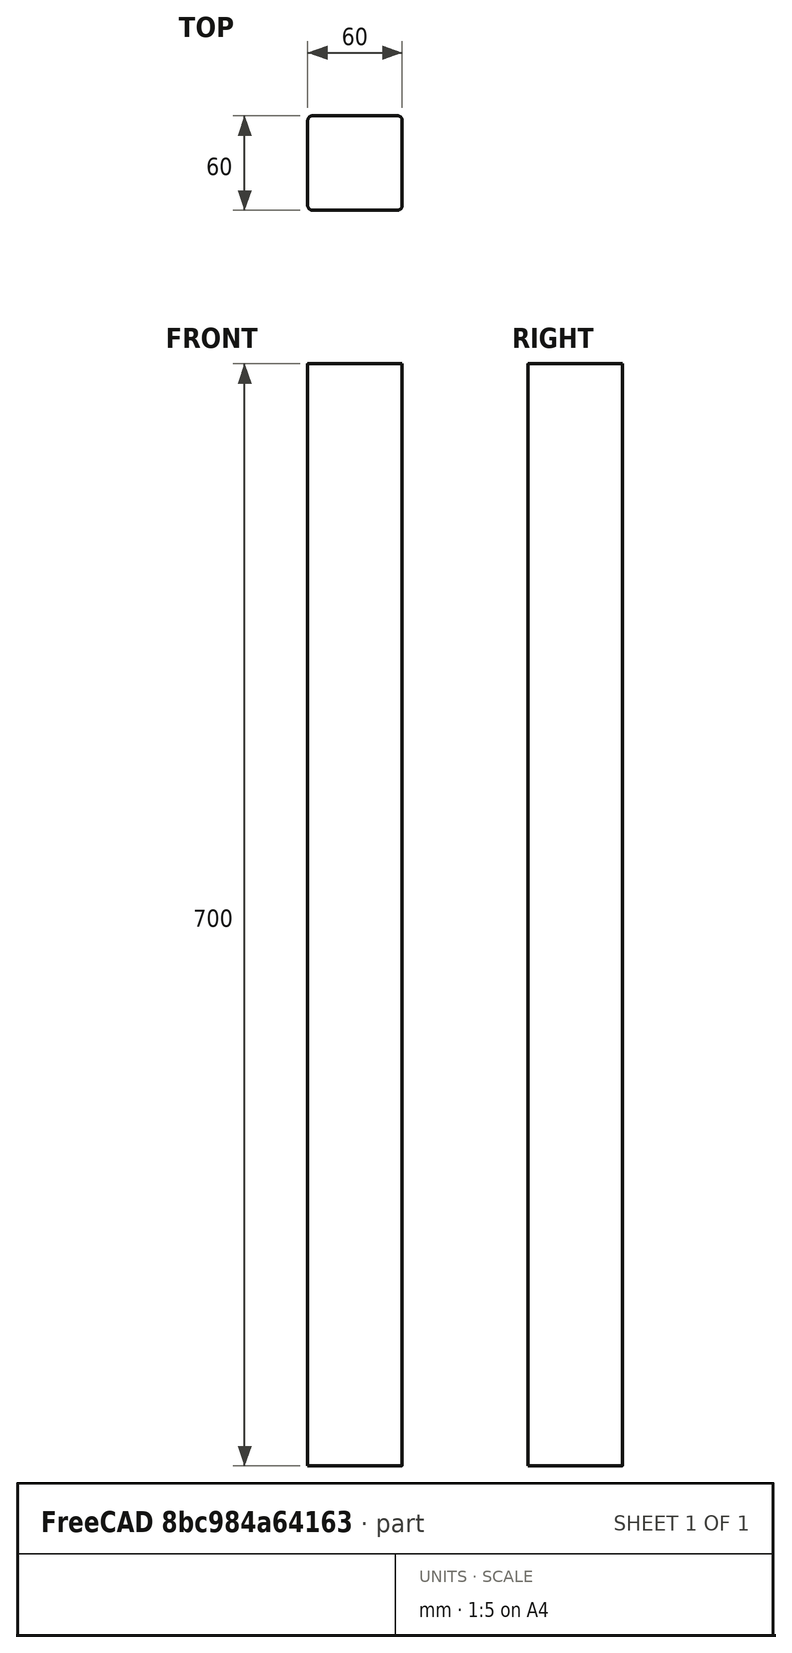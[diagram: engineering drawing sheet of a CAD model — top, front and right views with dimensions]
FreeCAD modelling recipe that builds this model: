
FCSTD DOCUMENT  (FreeCAD 0.19R)
Label: column_60_60
License: All rights reserved
LicenseURL: http://en.wikipedia.org/wiki/All_rights_reserved
objects: PartDesign::CoordinateSystem×7, Sketcher::SketchObject×1, PartDesign::Pad×1, PartDesign::Body×1
note: 11 computed .brp shape members not serialized (recipe doc carries the construction recipe); baked Part::Feature solids carry a one-line shape summary decoded from their .brp

FEATURE [PartDesign::CoordinateSystem] LCS_0
  AttacherType = Attacher::AttachEngine3D
  MapMode = 2
  Support = -> [X_Axis]
FEATURE [Sketcher::SketchObject] Sketch
  FullyConstrained = true
  MapMode = 5
  Support = -> [XY_Plane]
  sketch-geometry (8):
    g0: LineSegment StartX=-27 StartY=30 StartZ=0 EndX=27 EndY=30 EndZ=0
    g1: LineSegment StartX=30 StartY=27 StartZ=0 EndX=30 EndY=-27 EndZ=0
    g2: LineSegment StartX=27 StartY=-30 StartZ=0 EndX=-27 EndY=-30 EndZ=0
    g3: LineSegment StartX=-30 StartY=-27 StartZ=0 EndX=-30 EndY=27 EndZ=0
    g4: ArcOfCircle CenterX=-27 CenterY=27 CenterZ=0 NormalX=0 NormalY=0 NormalZ=1 AngleXU=0 Radius=3 StartAngle=1.5708 EndAngle=3.14159
    g5: ArcOfCircle CenterX=-27 CenterY=-27 CenterZ=0 NormalX=0 NormalY=0 NormalZ=1 AngleXU=0 Radius=3 StartAngle=3.14159 EndAngle=4.71239
    g6: ArcOfCircle CenterX=27 CenterY=-27 CenterZ=0 NormalX=0 NormalY=0 NormalZ=1 AngleXU=0 Radius=3 StartAngle=4.71239 EndAngle=6.28319
    g7: ArcOfCircle CenterX=27 CenterY=27 CenterZ=0 NormalX=0 NormalY=0 NormalZ=1 AngleXU=0 Radius=3 StartAngle=-1.394e-13 EndAngle=1.5708
  constraints (18):
    c: Horizontal(g2)
    c: Vertical(g3)
    c: Tangent(g3,g4) = 1.5708
    c: Tangent(g0,g4) = 1.5708
    c: Tangent(g3,g5) = 1.5708
    c: Tangent(g2,g5) = 1.5708
    c: Tangent(g2,g6) = 1.5708
    c: Tangent(g1,g6) = 1.5708
    c: Tangent(g1,g7) = 1.5708
    c: Tangent(g0,g7) = 1.5708
    c: Radius(g4) = 3
    c: Equal(g4,g7)
    c: Equal(g4,g6)
    c: Equal(g4,g5)
    c: DistanceY(g2,g0) = 60
    c: DistanceX(g3,g1) = 60
    c: Symmetric(g2,g0,g-1)
    c: Symmetric(g3,g1,g-2)
FEATURE [PartDesign::Pad] Pad
  Direction = (1,1,1)
  Length = 700
  Length2 = 100
  Profile = -> Sketch
  Type = 0
FEATURE [PartDesign::CoordinateSystem] LCS_bottom  label="LCS_bottom_left"
  AttacherType = Attacher::AttachEngine3D
  AttachmentOffset = pos=(0,25,0) rot=(0,0,1;0rad)
  MapMode = 5
  Placement = pos=(0,-30,25) rot=(1,0,0;1.5708rad)
  Support = -> [Pad]
FEATURE [PartDesign::CoordinateSystem] LCS_bottom_right
  AttacherType = Attacher::AttachEngine3D
  AttachmentOffset = pos=(0,25,0) rot=(0,0,1;0rad)
  MapMode = 5
  Placement = pos=(3.414e-13,30,25) rot=(0,0.707107,0.707107;3.14159rad)
  Support = -> [Pad]
FEATURE [PartDesign::CoordinateSystem] LCS_1
  AttacherType = Attacher::AttachEngine3D
  AttachmentOffset = pos=(0,25,0) rot=(0,0,1;0rad)
  MapMode = 5
  Placement = pos=(30,-4.789e-12,25) rot=(0.57735,0.57735,0.57735;2.0944rad)
  Support = -> [Pad]
FEATURE [PartDesign::CoordinateSystem] LCS_2
  AttacherType = Attacher::AttachEngine3D
  AttachmentOffset = pos=(0,-25,-30) rot=(0,0,1;0rad)
  MapMode = 7
  Placement = pos=(3,30,675) rot=(-0.57735,0.57735,0.57735;4.18879rad)
  Support = -> [Pad]
FEATURE [PartDesign::CoordinateSystem] LCS_3
  AttacherType = Attacher::AttachEngine3D
  AttachmentOffset = pos=(0,-25,-30) rot=(0,0,1;0rad)
  MapMode = 7
  Placement = pos=(30,-3,675) rot=(0,0.707107,0.707107;3.14159rad)
  Support = -> [Pad]
FEATURE [PartDesign::CoordinateSystem] LCS_4
  AttacherType = Attacher::AttachEngine3D
  AttachmentOffset = pos=(0,-25,-30) rot=(0,0,1;0rad)
  MapMode = 7
  Placement = pos=(-3,-30,675) rot=(0.57735,0.57735,0.57735;2.0944rad)
  Support = -> [Pad]
FEATURE [PartDesign::Body] ____________Body  label="ColumnBody"
  Group = -> [LCS_0,Sketch,Pad,LCS_bottom,LCS_bottom_right,LCS_1,LCS_2,LCS_3,LCS_4]
  Origin = -> Origin
  Tip = -> Pad
